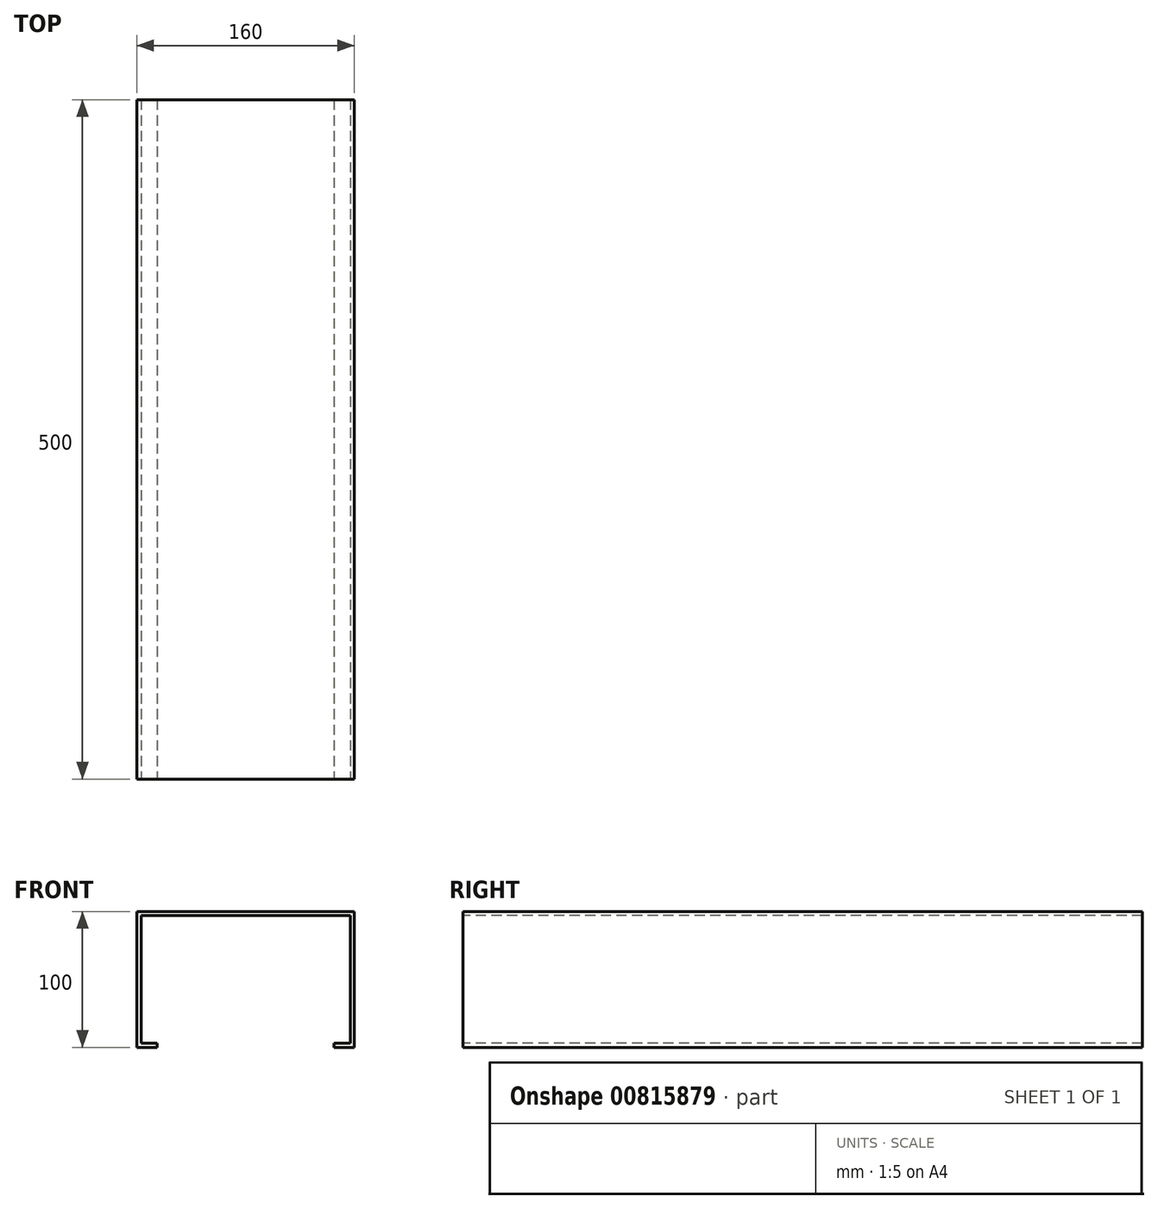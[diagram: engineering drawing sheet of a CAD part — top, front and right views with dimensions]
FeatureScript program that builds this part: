
annotation { "Feature Type Name" : "Feature", "Feature Type Description" : "" }
export const myFeature = defineFeature(function(context is Context, id is Id, definition is map)
    precondition{}
    {
        {
            var Q0;
            Q0=qCreatedBy(makeId("Front.planeOp"),FACE);
            var sketch = newSketch(context, id + "F0", { "sketchPlane" : qUnion([Q0])});
            skLineSegment(sketch, "E0", {"start": v(0, 0) * mm, "end": v(-15, 0) * mm});
            skLineSegment(sketch, "E1", {"start": v(-15, 0) * mm, "end": v(-15, 100) * mm});
            skLineSegment(sketch, "E2", {"start": v(-15, 100) * mm, "end": v(145, 100) * mm});
            skLineSegment(sketch, "E3", {"start": v(145, 100) * mm, "end": v(145, 0) * mm});
            skLineSegment(sketch, "E4", {"start": v(145, 0) * mm, "end": v(130, 0) * mm});
            skLineSegment(sketch, "E5.0", {"start": v(142, 3) * mm, "end": v(130, 3) * mm});
            skLineSegment(sketch, "E5.1", {"start": v(0, 3) * mm, "end": v(-12, 3) * mm});
            skLineSegment(sketch, "E5.2", {"start": v(-12, 3) * mm, "end": v(-12, 97) * mm});
            skLineSegment(sketch, "E5.3", {"start": v(-12, 97) * mm, "end": v(142, 97) * mm});
            skLineSegment(sketch, "E5.4", {"start": v(142, 97) * mm, "end": v(142, 3) * mm});
            skLineSegment(sketch, "E6", {"start": v(0, 3) * mm, "end": v(0, 0) * mm});
            skLineSegment(sketch, "E7", {"start": v(130, 3) * mm, "end": v(130, 0) * mm});
            skSolve(sketch);
        }
        {
            var Q0;
            Q0=qSketchRegion(id+"F0",true);
            extrude(context, id + "F1", {"entities" : qUnion([Q0]), "oppositeDirection" : true, "depth" : 500 * mm, "offsetDistance" : 25 * mm});
        }
    });
